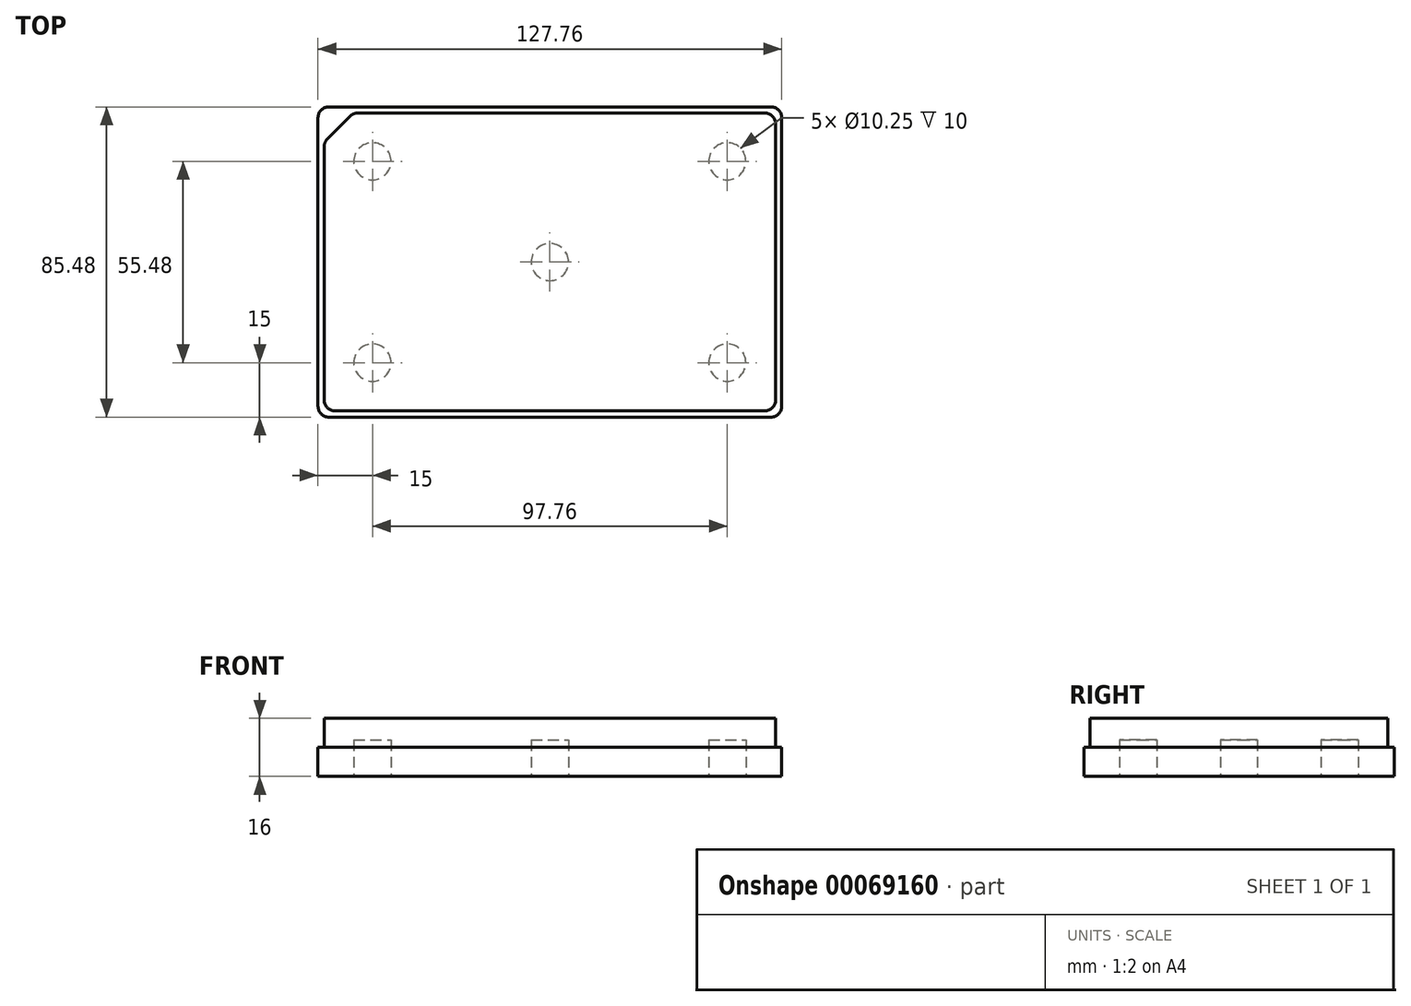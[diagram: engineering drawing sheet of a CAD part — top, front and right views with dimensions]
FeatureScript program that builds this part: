
annotation { "Feature Type Name" : "Feature", "Feature Type Description" : "" }
export const myFeature = defineFeature(function(context is Context, id is Id, definition is map)
    precondition{}
    {
        {
            var Q0;
            Q0=qCreatedBy(makeId("Top.planeOp"),FACE);
            var sketch = newSketch(context, id + "F0", { "sketchPlane" : qUnion([Q0])});
            skLineSegment(sketch, "E0.rect.bottom", {"start": v(63.88, -42.74) * mm, "end": v(-63.88, -42.74) * mm});
            skLineSegment(sketch, "E0.rect.top", {"start": v(63.88, 42.74) * mm, "end": v(-63.88, 42.74) * mm});
            skLineSegment(sketch, "E0.rect.left", {"start": v(63.88, -42.74) * mm, "end": v(63.88, 42.74) * mm});
            skLineSegment(sketch, "E0.rect.right", {"start": v(-63.88, -42.74) * mm, "end": v(-63.88, 42.74) * mm});
            skPoint(sketch, "E0.rect.middle", {"position": v(0, 0) * mm});
            skSolve(sketch);
        }
        {
            var Q0;
            Q0 = qSketchRegion(id + "F0", true);
            extrude(context, id + "F1", {"entities" : qUnion([Q0]), "depth" : 8 * mm});
        }
        {
            var Q0;
            Q0=makeQuery(id+"F1.opExtrude","CAP_FACE",FACE,{"disambiguationData":[OSD([sQuery(id+"F0.wireOp",EDGE,"E0.rect.bottom"),sQuery(id+"F0.wireOp",EDGE,"E0.rect.top"),sQuery(id+"F0.wireOp",EDGE,"E0.rect.left"),sQuery(id+"F0.wireOp",EDGE,"E0.rect.right")])],"isStart":false});
            var sketch = newSketch(context, id + "F2", { "sketchPlane" : qUnion([Q0])});
            skSolve(sketch);
        }
        {
            var Q0;
            Q0=makeQuery(id+"F2.imprint","IMPRINT",FACE,{"disambiguationData":[TD([[makeQuery(id+"F2.imprint","IMPRINT",EDGE,{"derivedFrom":makeQuery(id+"F1.opExtrude","CAP_EDGE",EDGE,{"disambiguationData":[OSD([sQuery(id+"F0.wireOp",EDGE,"E0.rect.bottom")])],"isStart":false})}),-1.0]])]});
            var sketch = newSketch(context, id + "F3", { "sketchPlane" : qUnion([Q0])});
            skLineSegment(sketch, "E1.rect.bottom", {"start": v(62.18, -41.04) * mm, "end": v(-62.18, -41.04) * mm});
            skLineSegment(sketch, "E1.rect.top", {"start": v(62.18, 41.04) * mm, "end": v(-62.18, 41.04) * mm});
            skLineSegment(sketch, "E1.rect.left", {"start": v(62.18, -41.04) * mm, "end": v(62.18, 41.04) * mm});
            skLineSegment(sketch, "E1.rect.right", {"start": v(-62.18, -41.04) * mm, "end": v(-62.18, 41.04) * mm});
            skPoint(sketch, "E1.rect.middle", {"position": v(0, 0) * mm});
            skSolve(sketch);
        }
        {
            var Q0;
            Q0 = qSketchRegion(id + "F3", true);
            extrude(context, id + "F4", {"entities" : qUnion([Q0]), "operationType" : NewBodyOperationType.ADD, "depth" : 8 * mm});
        }
        {
            var Q0;
            Q0=makeQuery(id+"F4.opExtrude","SWEPT_EDGE",EDGE,{"disambiguationData":[OSD([sQuery(id+"F3.wireOp",EDGE,"E1.rect.top"),sQuery(id+"F3.wireOp",EDGE,"E1.rect.right")])]});
            chamfer(context, id + "F5", {"entities" : qUnion([Q0]), "width" : 8 * mm, "tangentPropagation" : true});
        }
        {
            var Q0;
            Q0=makeQuery(id+"F1.opExtrude","SWEPT_EDGE",EDGE,{"disambiguationData":[OSD([sQuery(id+"F0.wireOp",EDGE,"E0.rect.top"),sQuery(id+"F0.wireOp",EDGE,"E0.rect.right")])]});
            var Q1;
            Q1=makeQuery(id+"F1.opExtrude","SWEPT_EDGE",EDGE,{"disambiguationData":[OSD([sQuery(id+"F0.wireOp",EDGE,"E0.rect.bottom"),sQuery(id+"F0.wireOp",EDGE,"E0.rect.right")])]});
            var Q2;
            Q2=makeQuery(id+"F1.opExtrude","SWEPT_EDGE",EDGE,{"disambiguationData":[OSD([sQuery(id+"F0.wireOp",EDGE,"E0.rect.bottom"),sQuery(id+"F0.wireOp",EDGE,"E0.rect.left")])]});
            var Q3;
            Q3=makeQuery(id+"F1.opExtrude","SWEPT_EDGE",EDGE,{"disambiguationData":[OSD([sQuery(id+"F0.wireOp",EDGE,"E0.rect.top"),sQuery(id+"F0.wireOp",EDGE,"E0.rect.left")])]});
            var Q4;
            {var subQ0=sQuery(id+"F3.wireOp",EDGE,"E1.rect.right");Q4=makeQuery(id+"F5.opChamfer","BLEND_EDGE",EDGE,{"blendedFrom":[makeQuery(id+"F4.opExtrude","SWEPT_EDGE",EDGE,{"disambiguationData":[OSD([sQuery(id+"F3.wireOp",EDGE,"E1.rect.top"),subQ0])]}),makeQuery(id+"F4.opExtrude","SWEPT_FACE",FACE,{"disambiguationData":[OSD([subQ0])]})],"blendedInto":[makeQuery(id+"F4.opExtrude","SWEPT_FACE",FACE,{"disambiguationData":[OSD([subQ0])]})]});}
            var Q5;
            Q5=makeQuery(id+"F4.opExtrude","SWEPT_EDGE",EDGE,{"disambiguationData":[OSD([sQuery(id+"F3.wireOp",EDGE,"E1.rect.bottom"),sQuery(id+"F3.wireOp",EDGE,"E1.rect.right")])]});
            var Q6;
            Q6=makeQuery(id+"F4.opExtrude","SWEPT_EDGE",EDGE,{"disambiguationData":[OSD([sQuery(id+"F3.wireOp",EDGE,"E1.rect.bottom"),sQuery(id+"F3.wireOp",EDGE,"E1.rect.left")])]});
            var Q7;
            Q7=makeQuery(id+"F4.opExtrude","SWEPT_EDGE",EDGE,{"disambiguationData":[OSD([sQuery(id+"F3.wireOp",EDGE,"E1.rect.top"),sQuery(id+"F3.wireOp",EDGE,"E1.rect.left")])]});
            var Q8;
            {var subQ0=sQuery(id+"F3.wireOp",EDGE,"E1.rect.top");Q8=makeQuery(id+"F5.opChamfer","BLEND_EDGE",EDGE,{"blendedFrom":[makeQuery(id+"F4.opExtrude","SWEPT_EDGE",EDGE,{"disambiguationData":[OSD([subQ0,sQuery(id+"F3.wireOp",EDGE,"E1.rect.right")])]}),makeQuery(id+"F4.opExtrude","SWEPT_FACE",FACE,{"disambiguationData":[OSD([subQ0])]})],"blendedInto":[makeQuery(id+"F4.opExtrude","SWEPT_FACE",FACE,{"disambiguationData":[OSD([subQ0])]})]});}
            fillet(context, id + "F6", {"entities" : qUnion([Q0, Q1, Q2, Q3, Q4, Q5, Q6, Q7, Q8]), "radius" : 3 * mm, "tangentPropagation" : true, "allowEdgeOverflow" : false});
        }
        {
            var Q0;
            Q0=makeQuery(id+"F1.opExtrude","CAP_FACE",FACE,{"disambiguationData":[OSD([sQuery(id+"F0.wireOp",EDGE,"E0.rect.bottom"),sQuery(id+"F0.wireOp",EDGE,"E0.rect.top"),sQuery(id+"F0.wireOp",EDGE,"E0.rect.left"),sQuery(id+"F0.wireOp",EDGE,"E0.rect.right")])],"isStart":true});
            var sketch = newSketch(context, id + "F7", { "sketchPlane" : qUnion([Q0])});
            skCircle(sketch, "E2", {"center": v(0, 0) * mm, "radius": 5.12 * mm});
            skCircle(sketch, "E3", {"center": v(48.88, 27.74) * mm, "radius": 5.12 * mm});
            skCircle(sketch, "E4", {"center": v(48.88, -27.74) * mm, "radius": 5.12 * mm});
            skCircle(sketch, "E5", {"center": v(-48.88, -27.74) * mm, "radius": 5.12 * mm});
            skCircle(sketch, "E6", {"center": v(-48.88, 27.74) * mm, "radius": 5.12 * mm});
            skSolve(sketch);
        }
        {
            var Q0;
            Q0 = qSketchRegion(id + "F7", true);
            extrude(context, id + "F8", {"entities" : qUnion([Q0]), "operationType" : NewBodyOperationType.REMOVE, "oppositeDirection" : true, "depth" : 10 * mm});
        }
    });
